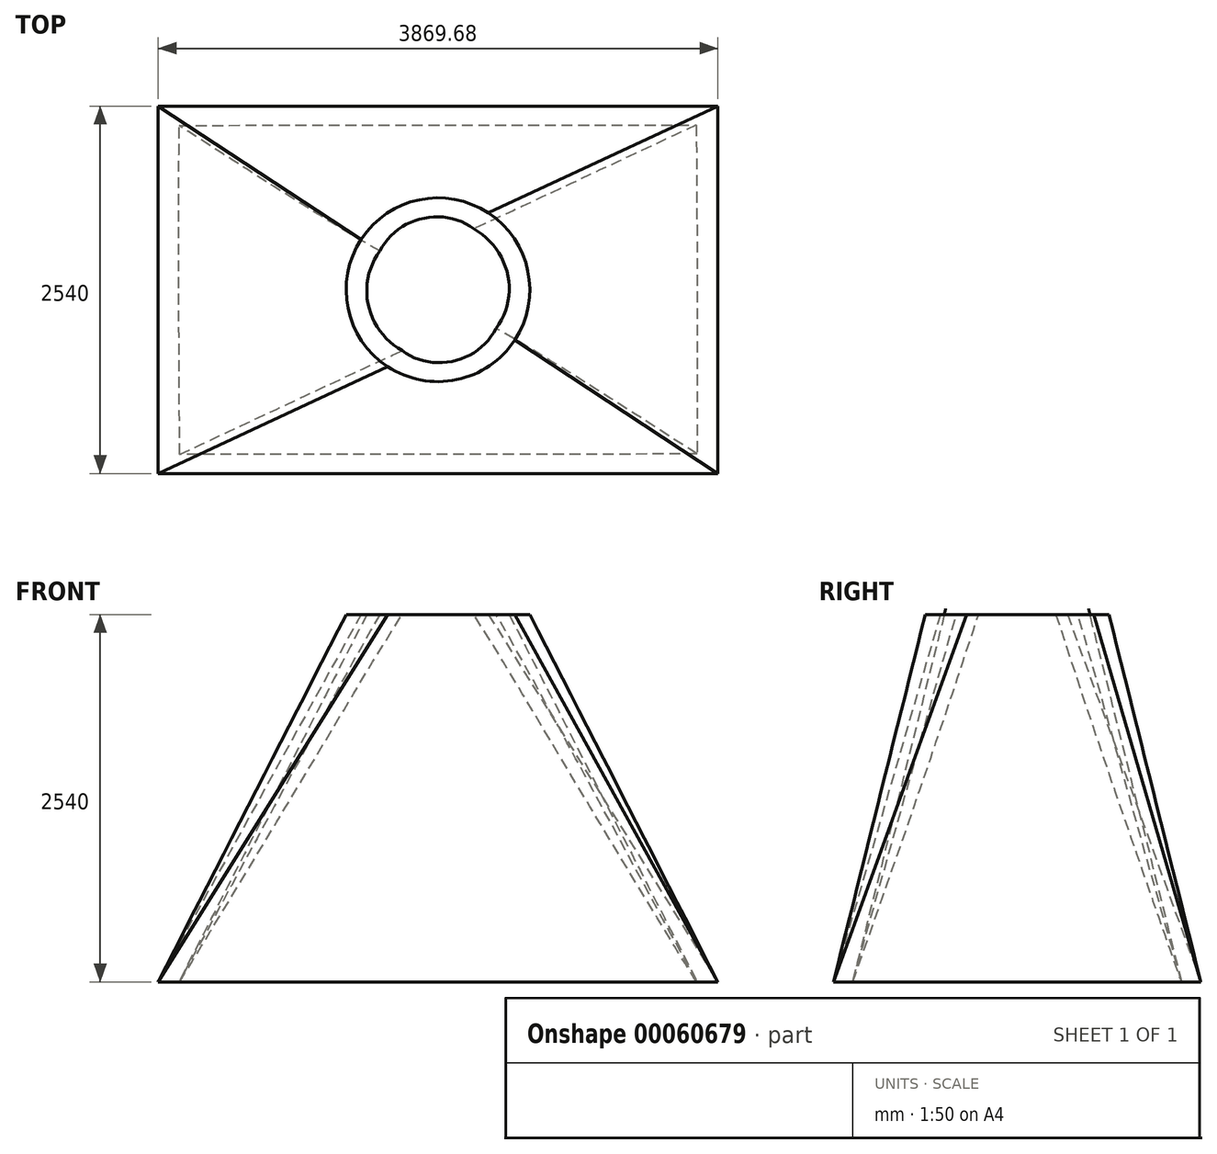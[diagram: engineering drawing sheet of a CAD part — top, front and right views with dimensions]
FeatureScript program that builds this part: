
annotation { "Feature Type Name" : "Feature", "Feature Type Description" : "" }
export const myFeature = defineFeature(function(context is Context, id is Id, definition is map)
    precondition{}
    {
        {
            var Q0;
            Q0=qCreatedBy(makeId("Top.planeOp"),FACE);
            var sketch = newSketch(context, id + "F0", { "sketchPlane" : qUnion([Q0])});
            skLineSegment(sketch, "E0.rect.bottom", {"start": v(-1934.84, 1270) * mm, "end": v(1934.84, 1270) * mm});
            skLineSegment(sketch, "E0.rect.top", {"start": v(-1934.84, -1270) * mm, "end": v(1934.84, -1270) * mm});
            skLineSegment(sketch, "E0.rect.left", {"start": v(-1934.84, 1270) * mm, "end": v(-1934.84, -1270) * mm});
            skLineSegment(sketch, "E0.rect.right", {"start": v(1934.84, 1270) * mm, "end": v(1934.84, -1270) * mm});
            skPoint(sketch, "E0.rect.middle", {"position": v(0, 0) * mm});
            skSolve(sketch);
        }
        {
            var Q0;
            Q0=makeQuery(id+"F0.imprint","IMPRINT",FACE,{"disambiguationData":[TD([[makeQuery(id+"F0.imprint","IMPRINT",EDGE,{"derivedFrom":sQuery(id+"F0.wireOp",EDGE,"E0.rect.bottom")}),-1.0]])]});
            cPlane(context, id + "F1", {"entities" : qUnion([Q0]), "cplaneType" : CPlaneType.OFFSET, "offset" : 2540 * mm, "width" : 152.4 * mm, "height" : 152.4 * mm});
        }
        {
            var Q0;
            Q0=qCreatedBy(id+"F1.planeOp",FACE);
            var sketch = newSketch(context, id + "F2", { "sketchPlane" : qUnion([Q0])});
            skCircle(sketch, "E1", {"center": v(0, 0) * mm, "radius": 635 * mm});
            skSolve(sketch);
        }
        {
            var Q0;
            Q0=makeQuery(id+"F2.imprint","IMPRINT",FACE,{"disambiguationData":[TD([[makeQuery(id+"F2.imprint","IMPRINT",EDGE,{"derivedFrom":sQuery(id+"F2.wireOp",EDGE,"E1")}),1.0]])]});
            var Q1;
            Q1=makeQuery(id+"F0.imprint","IMPRINT",FACE,{"disambiguationData":[TD([[makeQuery(id+"F0.imprint","IMPRINT",EDGE,{"derivedFrom":sQuery(id+"F0.wireOp",EDGE,"E0.rect.bottom")}),-1.0]])]});
            loft(context, id + "F3", {"sheetProfilesArray" : [{ "sheetProfileEntities" : qUnion([Q0]) }, { "sheetProfileEntities" : qUnion([Q1]) }]});
        }
        {
            var Q0;
            Q0=makeQuery(id+"F3.opLoft","CAP_FACE",FACE,{"disambiguationData":[OSD([makeQuery(id+"F2.imprint","IMPRINT",FACE,{"disambiguationData":[TD([[makeQuery(id+"F2.imprint","IMPRINT",EDGE,{"derivedFrom":sQuery(id+"F2.wireOp",EDGE,"E1")}),1.0]])]})])],"isStart":true});
            var Q1;
            Q1=makeQuery(id+"F3.opLoft","CAP_FACE",FACE,{"disambiguationData":[OSD([makeQuery(id+"F0.imprint","IMPRINT",FACE,{"disambiguationData":[TD([[makeQuery(id+"F0.imprint","IMPRINT",EDGE,{"derivedFrom":sQuery(id+"F0.wireOp",EDGE,"E0.rect.bottom")}),-1.0]])]})])],"isStart":true});
            shell(context, id + "F4", {"entities" : qUnion([Q0, Q1]), "thickness" : 127 * mm});
        }
    });
